# Revit family: X600_3_inch_Vertical_Series
name_source: partatom
category: Mechanical Equipment
revit_build: Autodesk Revit 2013 (Build: 20120221_2030(x64)
units: mm (PartAtom-declared; Revit-internal decimal feet)

## types (29) — shared parameters
Assembly Code = D2010900
Connecter Description = 3" NPT
Cord Type = UL Listed power and sensor cord
Default Elevation = 0"
Description = Vertical Discharge. Submersible Sewage Or Dewatering Non-Clog Pump for Hazardous Environment
Discharge Diameter = 3"
Discharge Radius = 1 1/2"
Height = 33 1/4"
Hertz = 60
Impeller Type (Default) = Ductile Iron Semi-Open
Installation Type = Floor Mounted
Insulation = Class F
Lead Wires Insulation = Class F
Length = 12 5/8"
Manufacturer = Zoeller
Masterformat Number = 33 36 16
Masterformat Title = Utility Septic Tank Effluent Pumps
Material = Cast Iron-Zoeller-Powder Coated Epoxy
Max. Water Temp. = 104 °F
Min. Recommended Fluid Level = 24"
Moisture Sensor = Moisture Sensing Probe (Requires a circuit in control panel)
Motor Design Letter = NEMA B
Motor Thermal Shutoff = Thermal Sensor (Requires a circuit in control panel)
Motor Type = FM and cCSAus rated Class 1, Division 1, Group C & D
O-Rings and Cover Gasket = Buna-N
Omniclass Table 23 Code = 23.60.30.21
Omniclass Table 23 Title = Pumps
Operation = Non-Automatic
Price = Prices may vary. Please consult Manufacturer Representative for most up-to-date price list.
Product Page URL = http://www.zoellerpumps.com
RPM = 1750
Solid Handling = 2 1/2" Spherical Solids
Tandem Seals = Standard
Type SOW Power Cord Length = 300"
URL = http://www.zoellerpumps.com
Warranty Information = 18 Months (Limited)
Waste Connection = Yes
Width = 17 9/16"

## per-type parameters (varying)
| type | Apparent Load | Flow X611-X651 @5', X661 @ 10' | Full Load Amps | Locked Rotor Amps | Maximum Head | Model | Motor | Phase | Type | Voltage |
| X611 - 230V 1Ph | 1587 VA | 250 GPM | 7 A | 48 A | 264" | X611 | 1.0 HP | 1 | Capacitor Star/Capacitor Run | 230 V |
| X611 - 200V 3Ph | 8 VA | 250 GPM | 4 A | 32 A | 264" | X611 | 1.0 HP | 3 | 3 Phase | 200 V |
| X611 - 230V 3Ph | 828 VA | 250 GPM | 4 A | 28 A | 264" | X611 | 1.0 HP | 3 | 3 Phase | 230 V |
| X611 - 460V 3Ph | 828 VA | 250 GPM | 2 A | 14 A | 264" | X611 | 1.0 HP | 3 | 3 Phase | 460 V |
| X611 - 575V 3Ph | 805 VA | 250 GPM | 1 A | 12 A | 264" | X611 | 1.0 HP | 3 | 3 Phase | 575 V |
| X621 - 230V 1Ph | 2047 VA | 320 GPM | 9 A | 48 A | 348" | X621 | 1.5 HP | 1 | Capacitor Star/Capacitor Run | 230 V |
| X621 - 200V 3Ph | 1160 VA | 320 GPM | 6 A | 32 A | 348" | X621 | 1.5 HP | 3 | 3 Phase | 200 V |
| X621 - 230V 3Ph | 1173 VA | 320 GPM | 5 A | 28 A | 348" | X621 | 1.5 HP | 3 | 3 Phase | 230 V |
| X621 - 460V 3Ph | 1196 VA | 320 GPM | 3 A | 14 A | 348" | X621 | 1.5 HP | 3 | 3 Phase | 460 V |
| X621 - 575V 3Ph | 1150 VA | 320 GPM | 2 A | 12 A | 348" | X621 | 1.5 HP | 3 | 3 Phase | 575 V |
| X631 - 230V 1Ph | 3335 VA | 390 GPM | 15 A | 86 A | 408" | X631 | 2.0 HP | 1 | Capacitor Star/Capacitor Run | 230 V |
| X631 - 200V 3Ph | 1560 VA | 390 GPM | 8 A | 46 A | 408" | X631 | 2.0 HP | 3 | 3 Phase | 200 V |
| X631 - 230V 3Ph | 1564 VA | 390 GPM | 7 A | 41 A | 408" | X631 | 2.0 HP | 3 | 3 Phase | 230 V |
| X631 - 460V 3Ph | 1564 VA | 390 GPM | 3 A | 21 A | 408" | X631 | 2.0 HP | 3 | 3 Phase | 460 V |
| X631 - 575V 3Ph | 1553 VA | 390 GPM | 3 A | 16 A | 408" | X631 | 2.0 HP | 3 | 3 Phase | 575 V |
| X641 - 230V 1Ph | 3910 VA | 420 GPM | 17 A | 86 A | 474" (1 Ph), 528" (3 Ph) | X641 | 3.0 HP | 1 | Capacitor Star/Capacitor Run | 230 V |
| X641 - 200V 3Ph | 2200 VA | 460 GPM | 11 A | 46 A | 474" (1 Ph), 528" (3 Ph) | X641 | 3.0 HP | 3 | 3 Phase | 200 V |
| X641 - 230V 3Ph | 2208 VA | 460 GPM | 10 A | 41 A | 474" (1 Ph), 528" (3 Ph) | X641 | 3.0 HP | 3 | 3 Phase | 230 V |
| X641 - 460V 3Ph | 2208 VA | 460 GPM | 5 A | 21 A | 474" (1 Ph), 528" (3 Ph) | X641 | 3.0 HP | 3 | 3 Phase | 460 V |
| X641 - 575V 3Ph | 2243 VA | 460 GPM | 4 A | 16 A | 474" (1 Ph), 528" (3 Ph) | X641 | 3.0 HP | 3 | 3 Phase | 575 V |
| X651 - 230V 1Ph | 6440 VA | 475 GPM | 28 A | 139 A | 558" (1 Ph), 648" (3 Ph) | X651 | 5.0 HP | 1 | Capacitor Star/Capacitor Run | 230 V |
| X651 - 200V 3Ph | 3500 VA | 533 GPM | 18 A | 64 A | 558" (1 Ph), 648" (3 Ph) | X651 | 5.0 HP | 3 | 3 Phase | 200 V |
| X651 - 230V 3Ph | 3496 VA | 533 GPM | 15 A | 58 A | 558" (1 Ph), 648" (3 Ph) | X651 | 5.0 HP | 3 | 3 Phase | 230 V |
| X651 - 460V 3Ph | 3496 VA | 533 GPM | 8 A | 29 A | 558" (1 Ph), 648" (3 Ph) | X651 | 5.0 HP | 3 | 3 Phase | 460 V |
| X651 - 575V 3Ph | 3508 VA | 533 GPM | 6 A | 23 A | 558" (1 Ph), 648" (3 Ph) | X651 | 5.0 HP | 3 | 3 Phase | 575 V |
| X661 - 200V 3Ph | 5600 VA | 600 GPM | 28 A | 83 A | 780" | X661 | 7.5 HP | 3 | 3 Phase | 200 V |
| X661 - 230V 3Ph | 5290 VA | 600 GPM | 23 A | 72 A | 780" | X661 | 7.5 HP | 3 | 3 Phase | 230 V |
| X661 - 460V 3Ph | 5750 VA | 600 GPM | 13 A | 36 A | 780" | X661 | 7.5 HP | 3 | 3 Phase | 460 V |
| X661 - 575V 3Ph | 5405 VA | 600 GPM | 9 A | 29 A | 780" | X661 | 7.5 HP | 3 | 3 Phase | 575 V |

## geometry (parser evidence)
native form markers: Blend x4, Sweep x1
no freeform markers — native parametric forms only
